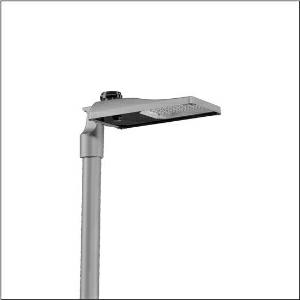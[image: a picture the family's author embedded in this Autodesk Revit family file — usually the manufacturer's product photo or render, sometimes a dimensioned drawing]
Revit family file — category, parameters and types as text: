
# Revit family: streetlight_sl_31_mini___st1_0a_5xh2d3bm08ja_c740
name_source: partatom
category: Lighting Fixtures
units: mm (PartAtom-declared; Revit-internal decimal feet)

## family parameters
Cut with Voids When Loaded = No
Host = Face
Light Source = No
Part Type = Normal
Room Calculation Point = No
Round Connector Dimension = Use Diameter
Shared = No

## types (1)
- --- (1 x LED, 12270 lm, 82.5 W, 3000K)
    Apparent Load = 83 VA
    CIE Flux Codes = 40 73 97 100 100
    Color Rendering = 70
    Color Temperature = 3000K
    Default Elevation = 1800 mm
    Description = Streetlight SL 31 mini NEMA (7pin) mast luminaire for post-top, side-entry; light control with lens of PMMA; light distribution: ST1.0a, direct asymmetric distribution, for standard-compliant lighting for roads and squares; LED: luminous flux: 12.270lm, light colour: 730, colour temperature: 3000K; luminous efficacy: 148,7lm/W; control: pre-setting: linear dimming characteristic, flexible luminous flux parameterisation, time-dependent luminous flux control, constant luminous flux control, intelligent temperature release in ECG and LED module, overheat protection; luminaire housing, of diecast aluminium, Siteco® metallic grey (DB 702S), corrosivity category C5 high according to DIN EN ISO 12944; cover of toughened safety glass, transparent, mast flange of diecast aluminium, Siteco® metallic grey (DB 702S), spigot size: 76/60mm, mast flange included unmounted; with cable H07RN-F 3x 1.5mm², cable length: 10,5m, connection cable pre-assembled; mains connection: 220..240V, AC, 50/60Hz; power consumption (at start of service life): 82,5W / (at end of service life): 90,1W / (with reduced operation 50%): 36,8W; protection rating (complete): IP66; insulation class (complete): insulation class I (protective earthing); impact resistance: IK09; certification: CE, ENEC, ENEC+, VDE, UKCA; permissible operating ambient temperature for outdoor applications: -40..+50°C; packaging unit: 1 piece

Light Distribution: ST1.0a
    Height = 76 mm
    Lamp = 1 x LED
    Lamp Light Flux = 12270 lm
    Lamp Power = 82.5 W
    Lamp count = 1
    Length = 547 mm
    Luminous efficacy = 149 lm/W
    Manufacturer = Siteco
    ModVariant = No
    Model = 5XH2D3BM08JA
    Number of Poles = 1
    OnlyDefault = Yes
    Power Factor = 1
    Product Name = Streetlight SL 31 mini | ST1.0a
    Product group = mast luminaire | pylon top
    ProductGroupID = 6100
    Protection Class = Protection class I
    Protection Degree = IP 66
    RLX_Detail_Level = 1
    RLX_Emergency_Light_Flux = 0 lm
    RLX_Emergency_Type = 0
    RLX_Emergency_Type_DB = No
    RlxData = <blob elided: 40329 chars, md5=d6cc6440>
    Socket = socket
    Standby Power = 0 W
    System Light Flux = 12270 lm
    System Power = 83 W
    Type Comments = factory setting: luminous flux: 100 % | dim-lin: 254 | 870 mA
    Type Image = l_1300324.jpg
    URL = http://relux.com
    VarID = @adj_071117
    Voltage = 0 V
    Weight = 0.00 kg
    Width = 265 mm

## geometry (parser evidence)
native form markers: Blend x4, Sweep x10
no freeform markers — native parametric forms only
